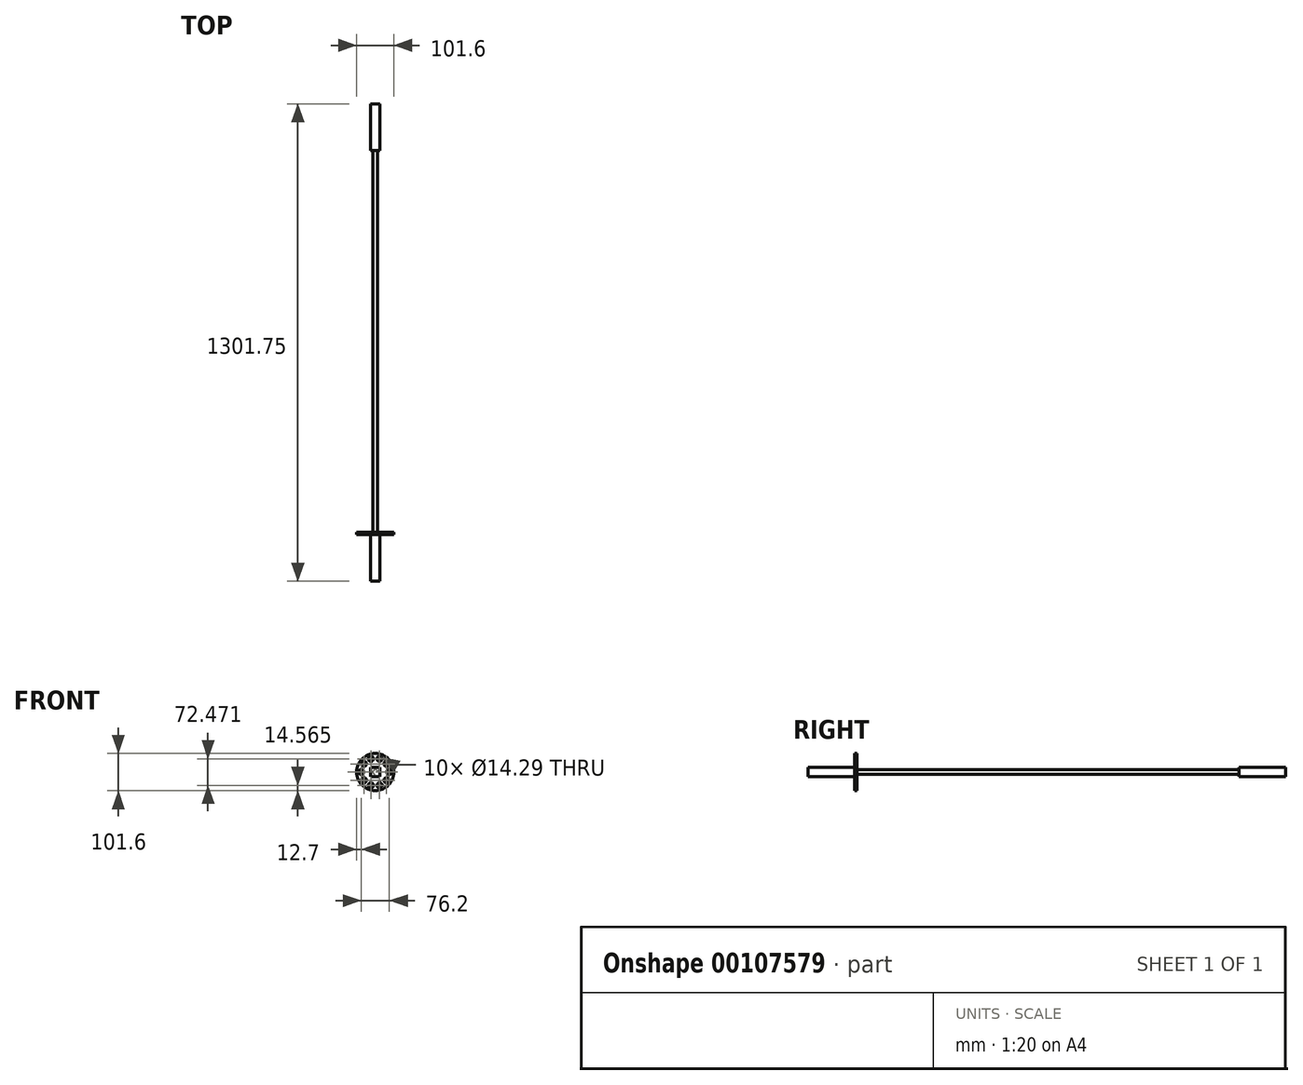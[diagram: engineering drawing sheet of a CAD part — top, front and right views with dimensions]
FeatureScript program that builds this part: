
annotation { "Feature Type Name" : "Feature", "Feature Type Description" : "" }
export const myFeature = defineFeature(function(context is Context, id is Id, definition is map)
    precondition{}
    {
        {
            var Q0;
            Q0=qCreatedBy(makeId("Front.planeOp"),FACE);
            var sketch = newSketch(context, id + "F0", { "sketchPlane" : qUnion([Q0])});
            skCircle(sketch, "E0", {"center": v(0, 0) * mm, "radius": 50.8 * mm});
            skCircle(sketch, "E1", {"center": v(0, 0) * mm, "radius": 38.1 * mm, "construction": true});
            skCircle(sketch, "E2", {"center": v(38.1, 0) * mm, "radius": 7.14 * mm});
            skCircle(sketch, "E3.1.0", {"center": v(30.82, 22.4) * mm, "radius": 7.14 * mm});
            skCircle(sketch, "E3.2.0", {"center": v(11.77, 36.24) * mm, "radius": 7.14 * mm});
            skCircle(sketch, "E3.3.0", {"center": v(-11.77, 36.24) * mm, "radius": 7.14 * mm});
            skCircle(sketch, "E3.4.0", {"center": v(-30.82, 22.4) * mm, "radius": 7.14 * mm});
            skCircle(sketch, "E3.5.0", {"center": v(-38.1, 0) * mm, "radius": 7.14 * mm});
            skCircle(sketch, "E3.6.0", {"center": v(-30.82, -22.4) * mm, "radius": 7.14 * mm});
            skCircle(sketch, "E3.7.0", {"center": v(-11.77, -36.24) * mm, "radius": 7.14 * mm});
            skCircle(sketch, "E3.8.0", {"center": v(11.77, -36.24) * mm, "radius": 7.14 * mm});
            skCircle(sketch, "E3.9.0", {"center": v(30.82, -22.4) * mm, "radius": 7.14 * mm});
            skSolve(sketch);
        }
        {
            var Q0;
            Q0=makeQuery(id+"F0.imprint","IMPRINT",FACE,{"disambiguationData":[TD([[makeQuery(id+"F0.imprint","IMPRINT",EDGE,{"derivedFrom":sQuery(id+"F0.wireOp",EDGE,"E0")}),1.0]])]});
            extrude(context, id + "F1", {"entities" : qUnion([Q0]), "depth" : 6.35 * mm});
        }
        {
            var Q0;
            Q0=makeQuery(id+"F1.opExtrude","CAP_FACE",FACE,{"disambiguationData":[OSD([sQuery(id+"F0.wireOp",EDGE,"E0"),sQuery(id+"F0.wireOp",EDGE,"E2"),sQuery(id+"F0.wireOp",EDGE,"E3.1.0"),sQuery(id+"F0.wireOp",EDGE,"E3.2.0"),sQuery(id+"F0.wireOp",EDGE,"E3.3.0"),sQuery(id+"F0.wireOp",EDGE,"E3.4.0"),sQuery(id+"F0.wireOp",EDGE,"E3.5.0"),sQuery(id+"F0.wireOp",EDGE,"E3.6.0"),sQuery(id+"F0.wireOp",EDGE,"E3.7.0"),sQuery(id+"F0.wireOp",EDGE,"E3.8.0"),sQuery(id+"F0.wireOp",EDGE,"E3.9.0")])],"isStart":false});
            var sketch = newSketch(context, id + "F2", { "sketchPlane" : qUnion([Q0])});
            skLineSegment(sketch, "E4.bottom", {"start": v(12.7, -12.7) * mm, "end": v(-12.7, -12.7) * mm});
            skLineSegment(sketch, "E4.top", {"start": v(12.7, 12.7) * mm, "end": v(-12.7, 12.7) * mm});
            skLineSegment(sketch, "E4.left", {"start": v(12.7, -12.7) * mm, "end": v(12.7, 12.7) * mm});
            skLineSegment(sketch, "E4.right", {"start": v(-12.7, -12.7) * mm, "end": v(-12.7, 12.7) * mm});
            skPoint(sketch, "E4.middle", {"position": v(0, 0) * mm});
            skSolve(sketch);
        }
        {
            var Q0;
            Q0 = qSketchRegion(id + "F2", true);
            extrude(context, id + "F3", {"entities" : qUnion([Q0]), "operationType" : NewBodyOperationType.ADD, "depth" : 127 * mm});
        }
        {
            var Q0;
            Q0=makeQuery(id+"F1.opExtrude","CAP_FACE",FACE,{"disambiguationData":[OSD([sQuery(id+"F0.wireOp",EDGE,"E0"),sQuery(id+"F0.wireOp",EDGE,"E2"),sQuery(id+"F0.wireOp",EDGE,"E3.1.0"),sQuery(id+"F0.wireOp",EDGE,"E3.2.0"),sQuery(id+"F0.wireOp",EDGE,"E3.3.0"),sQuery(id+"F0.wireOp",EDGE,"E3.4.0"),sQuery(id+"F0.wireOp",EDGE,"E3.5.0"),sQuery(id+"F0.wireOp",EDGE,"E3.6.0"),sQuery(id+"F0.wireOp",EDGE,"E3.7.0"),sQuery(id+"F0.wireOp",EDGE,"E3.8.0"),sQuery(id+"F0.wireOp",EDGE,"E3.9.0")])],"isStart":true});
            var sketch = newSketch(context, id + "F4", { "sketchPlane" : qUnion([Q0])});
            skCircle(sketch, "E5", {"center": v(0, 0) * mm, "radius": 6.35 * mm});
            skSolve(sketch);
        }
        {
            var Q0;
            Q0=makeQuery(id+"F4.imprint","IMPRINT",FACE,{"disambiguationData":[TD([[makeQuery(id+"F4.imprint","IMPRINT",EDGE,{"derivedFrom":sQuery(id+"F4.wireOp",EDGE,"E5")}),1.0]])]});
            var Q1;
            Q1=sQuery(id+"F4.wireOp",EDGE,"E5");
            extrude(context, id + "F5", {"entities" : qUnion([Q0]), "operationType" : NewBodyOperationType.ADD, "surfaceEntities" : qUnion([Q1]), "depth" : 1041.4 * mm});
        }
        {
            var Q0;
            Q0=makeQuery(id+"F5.opExtrude","CAP_FACE",FACE,{"disambiguationData":[OSD([sQuery(id+"F4.wireOp",EDGE,"E5")])],"isStart":false});
            var sketch = newSketch(context, id + "F6", { "sketchPlane" : qUnion([Q0])});
            skLineSegment(sketch, "E6.bottom", {"start": v(12.7, -12.7) * mm, "end": v(-12.7, -12.7) * mm});
            skLineSegment(sketch, "E6.top", {"start": v(12.7, 12.7) * mm, "end": v(-12.7, 12.7) * mm});
            skLineSegment(sketch, "E6.left", {"start": v(12.7, -12.7) * mm, "end": v(12.7, 12.7) * mm});
            skLineSegment(sketch, "E6.right", {"start": v(-12.7, -12.7) * mm, "end": v(-12.7, 12.7) * mm});
            skPoint(sketch, "E6.middle", {"position": v(0, 0) * mm});
            skSolve(sketch);
        }
        {
            var Q0;
            Q0 = qSketchRegion(id + "F6", true);
            extrude(context, id + "F7", {"entities" : qUnion([Q0]), "operationType" : NewBodyOperationType.ADD, "depth" : 127 * mm});
        }
    });
